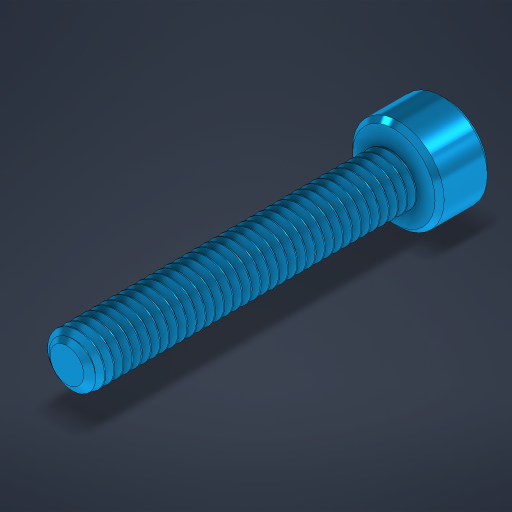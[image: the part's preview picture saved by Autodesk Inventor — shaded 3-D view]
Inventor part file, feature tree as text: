
AUTODESK INVENTOR PART (.ipt)
format: ipt  version: 2024 (Build 280153000, 153)  size: 1,250,816 bytes
history: native  units: in
note: dims shown in document units (in); Inventor stores cm internally (conversion verified against a paired STEP export)
features: chamfer x1
ambient origin geometry x8: Origin, YZ Plane, XZ Plane, XY Plane, X Axis, Y Axis, Z Axis, Center Point
bodies: Solid1 (feature_tree)
feature tree (1):
  chamfer  "Chamfer1"  [1 undecoded]
note: 1 required parameter value undecoded (feature->parameter linkage not recoverable at this tier; creation-order binding heuristic only, values carry confidence <= 0.55)
